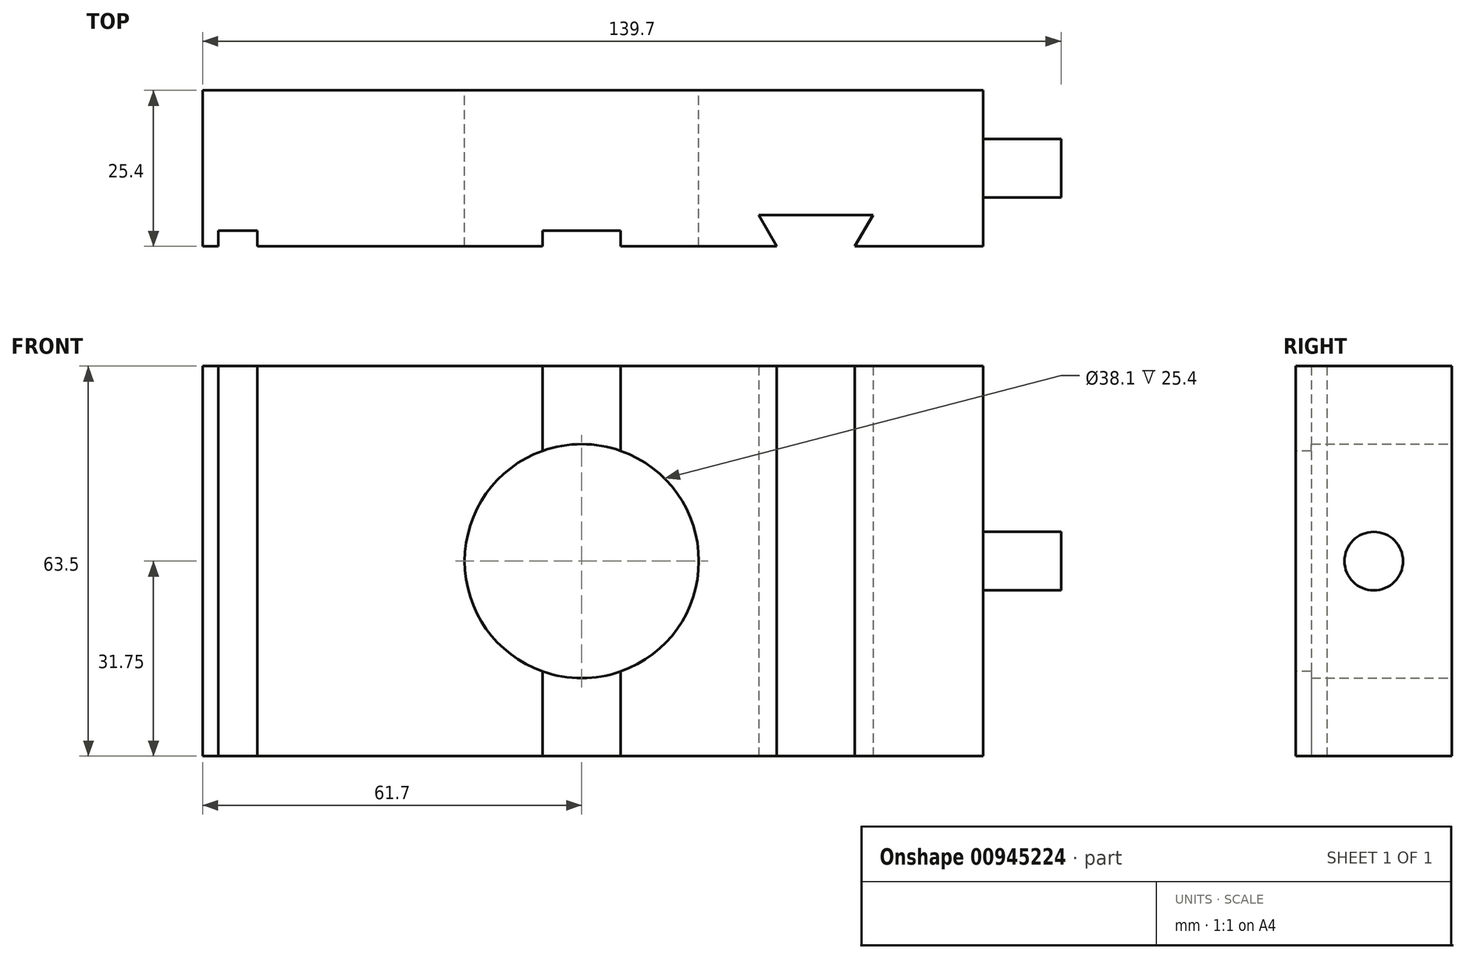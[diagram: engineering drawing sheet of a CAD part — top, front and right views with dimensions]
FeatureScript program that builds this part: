
annotation { "Feature Type Name" : "Feature", "Feature Type Description" : "" }
export const myFeature = defineFeature(function(context is Context, id is Id, definition is map)
    precondition{}
    {
        {
            var Q0;
            Q0=qCreatedBy(makeId("Front.planeOp"),FACE);
            var sketch = newSketch(context, id + "F0", { "sketchPlane" : qUnion([Q0])});
            skLineSegment(sketch, "E0.bottom", {"start": v(65.3, 31.75) * mm, "end": v(-61.7, 31.75) * mm});
            skLineSegment(sketch, "E0.top", {"start": v(65.3, -31.75) * mm, "end": v(-61.7, -31.75) * mm});
            skLineSegment(sketch, "E0.left", {"start": v(65.3, 31.75) * mm, "end": v(65.3, -31.75) * mm});
            skLineSegment(sketch, "E0.right", {"start": v(-61.7, 31.75) * mm, "end": v(-61.7, -31.75) * mm});
            skCircle(sketch, "E1", {"center": v(0, 0) * mm, "radius": 19.05 * mm});
            skSolve(sketch);
        }
        {
            var Q0;
            Q0=makeQuery(id+"F0.imprint","IMPRINT",FACE,{"disambiguationData":[TD([[makeQuery(id+"F0.imprint","IMPRINT",EDGE,{"derivedFrom":sQuery(id+"F0.wireOp",EDGE,"E0.bottom")}),1.0]])]});
            extrude(context, id + "F1", {"entities" : qUnion([Q0]), "depth" : 25.4 * mm, "offsetDistance" : 25.4 * mm});
        }
        {
            var Q0;
            Q0=makeQuery(id+"F1.opExtrude","CAP_FACE",FACE,{"disambiguationData":[OSD([sQuery(id+"F0.wireOp",EDGE,"E0.bottom"),sQuery(id+"F0.wireOp",EDGE,"E0.top"),sQuery(id+"F0.wireOp",EDGE,"E0.left"),sQuery(id+"F0.wireOp",EDGE,"E0.right"),sQuery(id+"F0.wireOp",EDGE,"WboAq6LC-goag-7pnR-1MJS-pq1X3Qhxo0ok")])],"isStart":false});
            var sketch = newSketch(context, id + "F2", { "sketchPlane" : qUnion([Q0])});
            skLineSegment(sketch, "E2.bottom", {"start": v(-59.16, 31.75) * mm, "end": v(-52.81, 31.75) * mm});
            skLineSegment(sketch, "E2.top", {"start": v(-59.16, -31.75) * mm, "end": v(-52.81, -31.75) * mm});
            skLineSegment(sketch, "E2.left", {"start": v(-59.16, 31.75) * mm, "end": v(-59.16, -31.75) * mm});
            skLineSegment(sketch, "E2.right", {"start": v(-52.81, 31.75) * mm, "end": v(-52.81, -31.75) * mm});
            skLineSegment(sketch, "E3", {"start": v(-6.35, 31.75) * mm, "end": v(-6.35, -31.75) * mm});
            skLineSegment(sketch, "E4", {"start": v(-6.35, -31.75) * mm, "end": v(6.35, -31.75) * mm});
            skLineSegment(sketch, "E5", {"start": v(6.35, -31.75) * mm, "end": v(6.35, 31.75) * mm});
            skLineSegment(sketch, "E6", {"start": v(6.35, 31.75) * mm, "end": v(-6.35, 31.75) * mm});
            skPoint(sketch, "E7", {"position": v(0, 0) * mm});
            skLineSegment(sketch, "E8", {"start": v(0, 31.75) * mm, "end": v(0, -31.75) * mm, "construction": true});
            skSolve(sketch);
        }
        {
            var Q0;
            Q0=makeQuery(id+"F2.imprint","IMPRINT",FACE,{"disambiguationData":[TD([[makeQuery(id+"F2.imprint","IMPRINT",EDGE,{"derivedFrom":sQuery(id+"F2.wireOp",EDGE,"E2.bottom")}),1.0]])]});
            var Q1;
            {var subQ0=sQuery(id+"F2.wireOp",EDGE,"E4");Q1=makeQuery(id+"F2.imprint","IMPRINT",FACE,{"disambiguationData":[TD([[makeQuery(id+"F2.imprint","IMPRINT",EDGE,{"derivedFrom":subQ0}),-1.0]])]});}
            var Q2;
            {var subQ0=sQuery(id+"F2.wireOp",EDGE,"E6");Q2=makeQuery(id+"F2.imprint","IMPRINT",FACE,{"disambiguationData":[TD([[makeQuery(id+"F2.imprint","IMPRINT",EDGE,{"derivedFrom":subQ0}),1.0]])]});}
            extrude(context, id + "F3", {"entities" : qUnion([Q0, Q1, Q2]), "operationType" : NewBodyOperationType.REMOVE, "oppositeDirection" : true, "depth" : 2.54 * mm, "offsetDistance" : 25.4 * mm});
        }
        {
            var Q0;
            Q0=makeQuery(id+"F1.opExtrude","SWEPT_FACE",FACE,{"disambiguationData":[OSD([sQuery(id+"F0.wireOp",EDGE,"E0.top")])]});
            var sketch = newSketch(context, id + "F4", { "sketchPlane" : qUnion([Q0])});
            skLineSegment(sketch, "E9", {"start": v(31.75, 25.4) * mm, "end": v(28.82, 20.32) * mm});
            skLineSegment(sketch, "E10", {"start": v(28.82, 20.32) * mm, "end": v(47.38, 20.32) * mm});
            skLineSegment(sketch, "E11", {"start": v(47.38, 20.32) * mm, "end": v(44.45, 25.4) * mm});
            skLineSegment(sketch, "E12", {"start": v(44.45, 25.4) * mm, "end": v(31.75, 25.4) * mm});
            skLineSegment(sketch, "E13", {"start": v(38.1, 20.32) * mm, "end": v(38.1, 25.4) * mm, "construction": true});
            skSolve(sketch);
        }
        {
            var Q0;
            Q0=makeQuery(id+"F4.imprint","IMPRINT",FACE,{"disambiguationData":[TD([[makeQuery(id+"F4.imprint","IMPRINT",EDGE,{"derivedFrom":sQuery(id+"F4.wireOp",EDGE,"E9")}),1.0]])]});
            extrude(context, id + "F5", {"entities" : qUnion([Q0]), "operationType" : NewBodyOperationType.REMOVE, "oppositeDirection" : true, "depth" : 66.04 * mm, "offsetDistance" : 25.4 * mm});
        }
        {
            var Q0;
            Q0=makeQuery(id+"F1.opExtrude","SWEPT_FACE",FACE,{"disambiguationData":[OSD([sQuery(id+"F0.wireOp",EDGE,"E0.left")])]});
            var sketch = newSketch(context, id + "F6", { "sketchPlane" : qUnion([Q0])});
            skCircle(sketch, "E14", {"center": v(-12.7, 0) * mm, "radius": 4.76 * mm});
            skPoint(sketch, "E14.centerSnap0", {"position": v(-12.7, -31.75) * mm});
            skPoint(sketch, "E14.centerSnap1", {"position": v(-25.4, 0) * mm});
            skSolve(sketch);
        }
        {
            var Q0;
            Q0=makeQuery(id+"F6.imprint","IMPRINT",FACE,{"disambiguationData":[TD([[makeQuery(id+"F6.imprint","IMPRINT",EDGE,{"derivedFrom":sQuery(id+"F6.wireOp",EDGE,"E14")}),1.0]])]});
            extrude(context, id + "F7", {"entities" : qUnion([Q0]), "operationType" : NewBodyOperationType.ADD, "depth" : 12.7 * mm, "offsetDistance" : 25.4 * mm});
        }
    });
